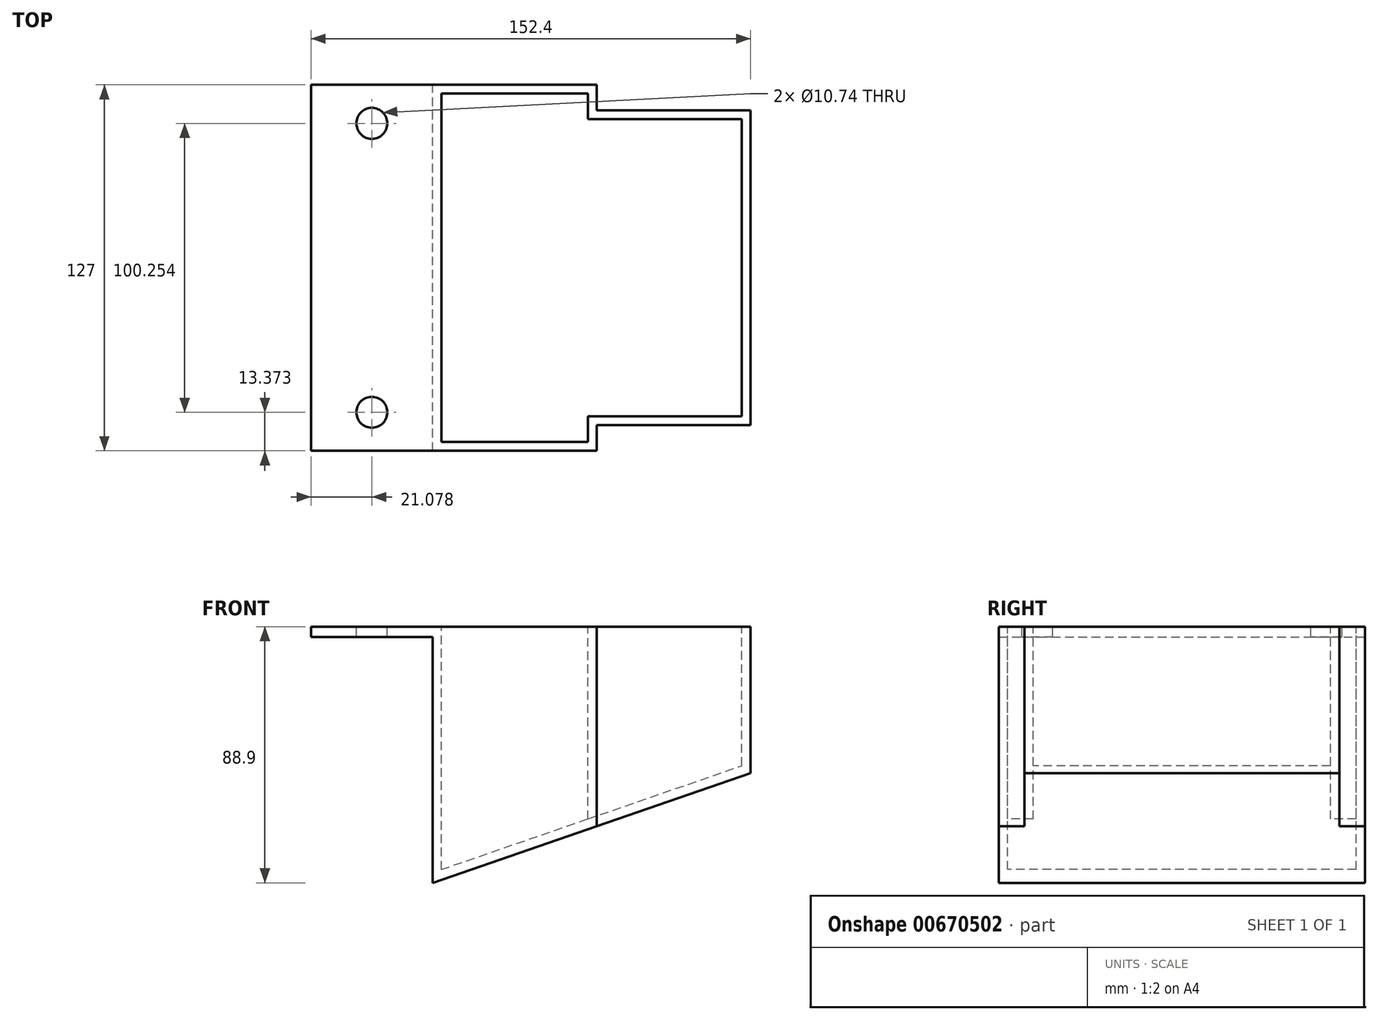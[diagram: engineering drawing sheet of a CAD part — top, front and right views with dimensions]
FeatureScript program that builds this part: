
annotation { "Feature Type Name" : "Feature", "Feature Type Description" : "" }
export const myFeature = defineFeature(function(context is Context, id is Id, definition is map)
    precondition{}
    {
        {
            var Q0;
            Q0=qCreatedBy(makeId("Top.planeOp"),FACE);
            var sketch = newSketch(context, id + "F0", { "sketchPlane" : qUnion([Q0])});
            skLineSegment(sketch, "E0", {"start": v(-42.16, 63.5) * mm, "end": v(-42.16, -63.5) * mm});
            skLineSegment(sketch, "E1", {"start": v(0, -63.5) * mm, "end": v(0, 63.5) * mm});
            skLineSegment(sketch, "E2", {"start": v(-42.16, 63.5) * mm, "end": v(56.84, 63.5) * mm});
            skLineSegment(sketch, "E3.0", {"start": v(110.24, 54.61) * mm, "end": v(110.24, -54.61) * mm});
            skLineSegment(sketch, "E4", {"start": v(56.84, 54.61) * mm, "end": v(110.24, 54.61) * mm});
            skLineSegment(sketch, "E5", {"start": v(56.84, -54.61) * mm, "end": v(110.24, -54.61) * mm});
            skLineSegment(sketch, "E6", {"start": v(-42.16, -63.5) * mm, "end": v(56.84, -63.5) * mm});
            skLineSegment(sketch, "E7", {"start": v(56.84, 63.5) * mm, "end": v(56.84, 54.61) * mm});
            skLineSegment(sketch, "E8", {"start": v(56.84, -54.6) * mm, "end": v(56.84, -63.5) * mm});
            skLineSegment(sketch, "E9.0", {"start": v(53.8, 51.56) * mm, "end": v(107.19, 51.56) * mm});
            skLineSegment(sketch, "E9.1", {"start": v(53.8, 60.45) * mm, "end": v(53.8, 51.56) * mm});
            skLineSegment(sketch, "E9.2", {"start": v(107.19, 51.56) * mm, "end": v(107.19, -51.56) * mm});
            skLineSegment(sketch, "E9.4", {"start": v(53.8, -51.56) * mm, "end": v(107.19, -51.56) * mm});
            skLineSegment(sketch, "E9.5", {"start": v(53.8, -51.56) * mm, "end": v(53.8, -60.45) * mm});
            skLineSegment(sketch, "E10.trimOffspring", {"start": v(3.05, 60.45) * mm, "end": v(53.8, 60.45) * mm});
            skLineSegment(sketch, "E11.trimOffspring", {"start": v(3.05, -60.45) * mm, "end": v(53.8, -60.45) * mm});
            skLineSegment(sketch, "E12", {"start": v(3.05, 60.45) * mm, "end": v(3.05, -60.45) * mm});
            skCircle(sketch, "E13", {"center": v(-21.08, 50.13) * mm, "radius": 5.37 * mm});
            skCircle(sketch, "E14.MirrorC", {"center": v(-21.08, -50.13) * mm, "radius": 5.37 * mm});
            skSolve(sketch);
        }
        {
            var Q0;
            {var subQ1=sQuery(id+"F0.wireOp",EDGE,"E1");Q0=makeQuery(id+"F0.imprint","IMPRINT",FACE,{"disambiguationData":[TD([[makeQuery(id+"F0.imprint","IMPRINT",EDGE,{"derivedFrom":subQ1}),-1.0]])]});}
            extrude(context, id + "F1", {"entities" : qUnion([Q0]), "oppositeDirection" : true, "depth" : 88.9 * mm, "offsetDistance" : 25.4 * mm});
        }
        {
            var Q0;
            Q0=makeQuery(id+"F1.opExtrude","SWEPT_FACE",FACE,{"disambiguationData":[OSD([sQuery(id+"F0.wireOp",EDGE,"E6")])]});
            var sketch = newSketch(context, id + "F2", { "sketchPlane" : qUnion([Q0])});
            skLineSegment(sketch, "E15.0", {"start": v(0, -88.9) * mm, "end": v(110.24, -88.9) * mm});
            skLineSegment(sketch, "E16.0", {"start": v(110.24, -88.9) * mm, "end": v(110.24, -50.8) * mm});
            skPoint(sketch, "E17.orphan", {"position": v(56.84, -88.9) * mm});
            skLineSegment(sketch, "E18", {"start": v(0, -88.9) * mm, "end": v(110.24, -50.8) * mm});
            skPoint(sketch, "E19.orphan", {"position": v(110.24, 0) * mm});
            skSolve(sketch);
        }
        {
            var Q0;
            {var subQ1=sQuery(id+"F2.wireOp",EDGE,"E15.0");var subQ2=sQuery(id+"F0.wireOp",EDGE,"E6");var subQ4=makeQuery(id+"F1.opExtrude","SWEPT_EDGE",EDGE,{"disambiguationData":[OSD([subQ2,sQuery(id+"F0.wireOp",EDGE,"E8")])]});var subQ5=makeQuery(id+"F2.imprint","INTERSECT",VERTEX,{"derivedFrom":[subQ4,subQ1]});Q0=makeQuery(id+"F2.imprint","IMPRINT",FACE,{"disambiguationData":[TD([[makeQuery(id+"F2.imprint","IMPRINT",EDGE,{"disambiguationData":[TD([[subQ5,1.0]])],"derivedFrom":subQ1}),1.0]])]});}
            var Q1;
            {var subQ3=sQuery(id+"F2.wireOp",EDGE,"E16.0");Q1=makeQuery(id+"F2.imprint","IMPRINT",FACE,{"disambiguationData":[TD([[makeQuery(id+"F2.imprint","IMPRINT",EDGE,{"derivedFrom":subQ3}),1.0]])]});}
            extrude(context, id + "F3", {"entities" : qUnion([Q0, Q1]), "operationType" : NewBodyOperationType.REMOVE, "oppositeDirection" : true, "depth" : 127 * mm, "offsetDistance" : 25.4 * mm});
        }
        {
            var Q0;
            {var subQ0=sQuery(id+"F0.wireOp",EDGE,"E0");Q0=makeQuery(id+"F0.imprint","IMPRINT",FACE,{"disambiguationData":[TD([[makeQuery(id+"F0.imprint","IMPRINT",EDGE,{"derivedFrom":subQ0}),1.0]])]});}
            extrude(context, id + "F4", {"entities" : qUnion([Q0]), "operationType" : NewBodyOperationType.ADD, "oppositeDirection" : true, "depth" : 3.56 * mm, "offsetDistance" : 25.4 * mm});
        }
        {
            var Q0;
            Q0=makeQuery(id+"F0.imprint","IMPRINT",FACE,{"disambiguationData":[TD([[makeQuery(id+"F0.imprint","IMPRINT",EDGE,{"derivedFrom":sQuery(id+"F0.wireOp",EDGE,"E9.0")}),-1.0]])]});
            var Q1;
            Q1=makeQuery(id+"F3.boolean.opBoolean","COPY",FACE,{"derivedFrom":makeQuery(id+"F3.opExtrude","SWEPT_FACE",FACE,{"disambiguationData":[OSD([sQuery(id+"F2.wireOp",EDGE,"E18")])]})});
            var Q2;
            Q2=makeQuery(id+"F3.boolean.opBoolean","COPY",FACE,{"derivedFrom":makeQuery(id+"F3.opExtrude","SWEPT_FACE",FACE,{"disambiguationData":[OSD([sQuery(id+"F2.wireOp",EDGE,"E18")])]})});
            extrude(context, id + "F5", {"entities" : qUnion([Q0]), "operationType" : NewBodyOperationType.ADD, "endBound" : BoundingType.UP_TO_SURFACE, "oppositeDirection" : true, "depth" : 25.4 * mm, "endBoundEntityFace" : qUnion([Q1]), "offsetDistance" : 25.4 * mm, "hasSecondDirection" : true, "secondDirectionBound" : SecondDirectionBoundingType.UP_TO_SURFACE, "secondDirectionOppositeDirection" : true, "secondDirectionDepth" : 25.4 * mm, "secondDirectionBoundEntityFace" : qUnion([Q2]), "hasSecondDirectionOffset" : true, "secondDirectionOffsetDistance" : 3.56 * mm});
        }
    });
